# Revit family: 854-00-002-DN50-300
name_source: partatom
category: Pipe Accessories
units: mm (PartAtom-declared; Revit-internal decimal feet)

## family parameters
Always vertical = No
Cut with Voids When Loaded = No
Part Type = Valve - Breaks Into
Round Connector Dimension = Use Diameter
Shared = No
Work Plane-Based = No

## types (7) — shared parameters
Body_wallthickness = 10 mm  [stored 0.0328084 ft]
DN050_PN16 = 854-050-00-1311
DN080_PN16 = 854-080-00-1311
DN100_PN16 = 854-100-00-1311
DN150_PN16 = 854-150-00-1311
DN200_PN16 = 854-200-00-1311
DN250_PN16 = 854-250-00-1311
DN300_PN16 = 854-300-00-1311
Description_ = AVK BALL FLOAT VALVE
Search_table = 854-00-002-DN50-300
URL product pages = https://www.avkvalves.com

## per-type parameters (varying)
| type | A | B | Ball_dia | Ball_dia_ref | Ball_dia_ref_2 | Body_wallthickness_ref | Body_wallthickness_ref_2 | Body_wallthickness_ref_3 | C | D | E | Fillet_length | Fillet_length_2 | Flange_OD | Flange_Thickness | G | ID | ID_ref | ID_ref_2 | L | Nominal Diameter (DN) | Rf_Dia | Side_Flange_length |
| DN050_PN16 | 110 mm  [stored 0.360892 ft] | 110 mm  [stored 0.360892 ft] | 310 mm | 310 mm | 124 mm  [stored 0.406824 ft] | 35 mm  [stored 0.114829 ft] | 70 mm  [stored 0.229659 ft] | 49 mm | 700 mm | 260 mm | 170 mm | 5 mm  [stored 0.0164042 ft] | 15 mm  [stored 0.0492126 ft] | 75 mm | 19 mm  [stored 0.062336 ft] | 150 mm | 25 mm  [stored 0.082021 ft] | 17 mm | 8 mm  [stored 0.0262467 ft] | 150 mm | 50 mm  [stored 0.164042 ft] | 42 mm  [stored 0.137795 ft] | 35 mm  [stored 0.114829 ft] |
| DN080_PN16 | 130 mm  [stored 0.426509 ft] | 145 mm | 360 mm | 360 mm | 144 mm | 50 mm  [stored 0.164042 ft] | 100 mm  [stored 0.328084 ft] | 70 mm  [stored 0.229659 ft] | 850 mm | 300 mm | 250 mm | 5 mm  [stored 0.0164042 ft] | 15 mm  [stored 0.0492126 ft] | 100 mm  [stored 0.328084 ft] | 19 mm  [stored 0.062336 ft] | 170 mm | 40 mm  [stored 0.131234 ft] | 27 mm | 13 mm | 180 mm | 80 mm  [stored 0.262467 ft] | 66 mm  [stored 0.216535 ft] | 50 mm  [stored 0.164042 ft] |
| DN100_PN16 | 140 mm  [stored 0.459318 ft] | 160 mm | 360 mm | 360 mm | 144 mm | 60 mm  [stored 0.19685 ft] | 120 mm  [stored 0.393701 ft] | 84 mm  [stored 0.275591 ft] | 1000 mm | 380 mm | 330 mm | 5 mm  [stored 0.0164042 ft] | 15 mm  [stored 0.0492126 ft] | 110 mm  [stored 0.360892 ft] | 19 mm  [stored 0.062336 ft] | 240 mm | 50 mm  [stored 0.164042 ft] | 33 mm | 17 mm | 190 mm | 100 mm  [stored 0.328084 ft] | 78 mm  [stored 0.255906 ft] | 60 mm  [stored 0.19685 ft] |
| DN150_PN16 | 180 mm | 210 mm | 460 mm | 460 mm | 184 mm | 85 mm  [stored 0.278871 ft] | 170 mm | 119 mm | 1250 mm | 470 mm | 480 mm | 8 mm  [stored 0.0262467 ft] | 23 mm | 142 mm | 19 mm  [stored 0.062336 ft] | 290 mm | 75 mm | 50 mm  [stored 0.164042 ft] | 25 mm  [stored 0.082021 ft] | 210 mm | 150 mm | 106 mm  [stored 0.347769 ft] | 80 mm  [stored 0.262467 ft] |
| DN200_PN16 | 220 mm | 270 mm | 460 mm | 460 mm | 184 mm | 110 mm  [stored 0.360892 ft] | 220 mm | 154 mm | 1500 mm | 570 mm | 650 mm | 10 mm  [stored 0.0328084 ft] | 30 mm  [stored 0.0984252 ft] | 170 mm | 20 mm  [stored 0.0656168 ft] | 350 mm | 100 mm  [stored 0.328084 ft] | 67 mm | 33 mm | 230 mm | 200 mm | 133 mm  [stored 0.436352 ft] | 100 mm  [stored 0.328084 ft] |
| DN250_PN16 | 250 mm | 330 mm | 460 mm | 460 mm | 184 mm | 135 mm  [stored 0.442913 ft] | 270 mm | 189 mm | 1800 mm | 650 mm | 810 mm | 10 mm  [stored 0.0328084 ft] | 30 mm  [stored 0.0984252 ft] | 200 mm | 22 mm  [stored 0.0721785 ft] | 400 mm | 125 mm  [stored 0.410105 ft] | 83 mm | 42 mm  [stored 0.137795 ft] | 250 mm | 250 mm | 160 mm | 120 mm  [stored 0.393701 ft] |
| DN300_PN16 | 300 mm | 380 mm | 460 mm | 460 mm | 184 mm | 160 mm | 320 mm | 224 mm | 2200 mm | 750 mm | 930 mm | 10 mm  [stored 0.0328084 ft] | 30 mm  [stored 0.0984252 ft] | 228 mm | 25 mm  [stored 0.082021 ft] | 450 mm | 150 mm | 100 mm  [stored 0.328084 ft] | 50 mm  [stored 0.164042 ft] | 270 mm | 300 mm | 185 mm | 140 mm  [stored 0.459318 ft] |

note: [stored X ft] marks values corroborated as IEEE doubles in the binary element streams (Revit-internal decimal feet)

## geometry (parser evidence)
native form markers: Extrusion x1, Sweep x5
no freeform markers — native parametric forms only
